# Revit family: Вазон «Консервативный»
name_source: partatom
category: Антураж
revit_build: Autodesk Revit 2017 (Build: 20160225_1515(x64)
units: mm (PartAtom-declared; Revit-internal decimal feet)

## family parameters
Всегда вертикально = Да
Источник визуального образа = Геометрия семейства
На основе рабочей плоскости = Нет
Общий = Нет
При загрузке вырезать с полостями = Нет
Точка расчета площади = Нет

## types (4) — shared parameters
ADSK_Код изделия = 8451
ADSK_Масса = 22.00 кг
ADSK_Наименование = Вазон «Консервативный» Большой
URL = https://hobbyka.ru
АDSK_Материал вазона = Гранит, выемка, полированный
Земля = Гравий
Изготовитель = Хоббика
zero-valued in all types: Высота

## per-type parameters (varying)
| type | ADSK__Размер_Высота | ADSK_Размер_Длина | ADSK_Размер_Ширина | b | Большой вазон | Стоимость |
| Вазон «Консервативный» Малый | 500 мм | 1500 мм | 700 мм | 400 мм | Да | 47380 $ |
| Вазон «Консервативный» Средний | 200 мм | 1000 мм | 300 мм | 200 мм | Нет | 22540 $ |
| Вазон «Консервативный» Средний плюс | 500 мм | 1500 мм | 700 мм | 500 мм | Да | 33810 $ |
| Вазон «Консервативный» Большой | 500 мм | 1500 мм | 700 мм | 400 мм | Да | 47380 $ |
